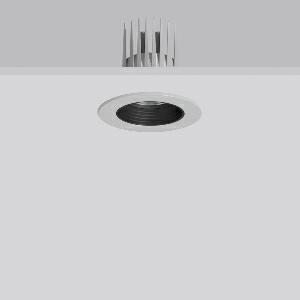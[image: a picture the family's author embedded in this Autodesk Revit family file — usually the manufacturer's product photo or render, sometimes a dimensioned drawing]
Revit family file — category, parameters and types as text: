
# Revit family: heledon_mini_e_901747_004_1_76_4984
name_source: partatom
category: Lighting Fixtures
units: mm (PartAtom-declared; Revit-internal decimal feet)

## family parameters
Cut with Voids When Loaded = No
Host = Face
Light Source = No
Part Type = Normal
Room Calculation Point = No
Round Connector Dimension = Use Diameter
Shared = No

## types (1)
- HELEDON mini E (1 x LED Modul 940, 2050 lm, 4000)
    Apparent Load = 20 VA
    Approval mark = CE
    CIE Flux Codes = 95 100 100 100 100
    Color Rendering = 92
    Color Temperature = 4000
    Default Elevation = 1800 mm
    Description = Series: HELEDON mini
Round recessed downlight. Housing: die-cast aluminium, powder-coated. Black plastic ring and recessed LED to prevent glare from the side. Optical assembly with lens made of plastic (polycarbonate) for the best homogeneous light distribution - can be changed without tools. Best colour rendering index Ra>90. Suitable for Recessed ceiling mounting. Installation without tools thanks to spring fastening system. Including separate LED converter with connecting cable 600 mm.High quality converter without flickering and stroboscopic effect. Through-wiring box (5 pole) available as accessory. The following accessories can be mounted without use of tools: interchangeable lenses, decorative glasses, honeycomb louvre, clear and frosted diffusers, white interchangeable plastic ring. 
Colour: silver
Diameter: 124 mm
Height: 3 mm
Cut-out diameter: 114 mm
Recess height: 170 mm
Luminaire: recess height: 120 mm
Lamp: LED
Socket: without socket
Colour temperature: 4000K
Colour rendering index (CRI): 92
System power: 20 W
Rated luminous flux: 2050 lm
Luminous efficiency: 103 lm/W
Control gear: Converter, dimmable, DALI
Protection class: II
Type of protection: IP 20
    Height = 0 mm  [stored 0 ft]
    Lamp = 1 x LED Modul 940
    Lamp Light Flux = 2050 lm
    Lamp count = 1
    Length = 124 mm  [stored 0.406824 ft]
    Lifetime = 50000 h
    Luminous efficacy = 103 lm/W
    Manufacturer = RZB
    ModVariant = No
    Model = 901747.004.1.76
    Mounting Place = Ceiling
    Mounting Type = Recessed
    Number of Poles = 1
    OnlyDefault = Yes
    Power Factor = 1
    Product Name = HELEDON mini E
    Product group = Recessed downlights
    ProductGroupID = 402
    Protection Class = Protection class II
    Protection Degree = IP 20
    RLX_Detail_Level = 1
    RLX_Emergency_Light_Flux = 0 lm
    RLX_Emergency_Type = 0
    RLX_Emergency_Type_DB = No
    RlxData = <blob elided: 133341 chars, md5=ffc4f360>
    Socket = socket
    Standby Power = 0 W
    System Light Flux = 2050 lm
    System Power = 20 W
    Type Comments = Product without accessories
    Type Image = 901656.004.jpg
    URL = http://relux.com
    VarID = ---
    Voltage = 230 V
    Voltage Range = 220-240 V
    Weight = 0.00 kg
    Width = 0 mm  [stored 0 ft]

note: [stored X ft] marks values corroborated as IEEE doubles in the binary element streams (Revit-internal decimal feet)

## geometry (parser evidence)
native form markers: Blend x4, Sweep x10
no freeform markers — native parametric forms only
